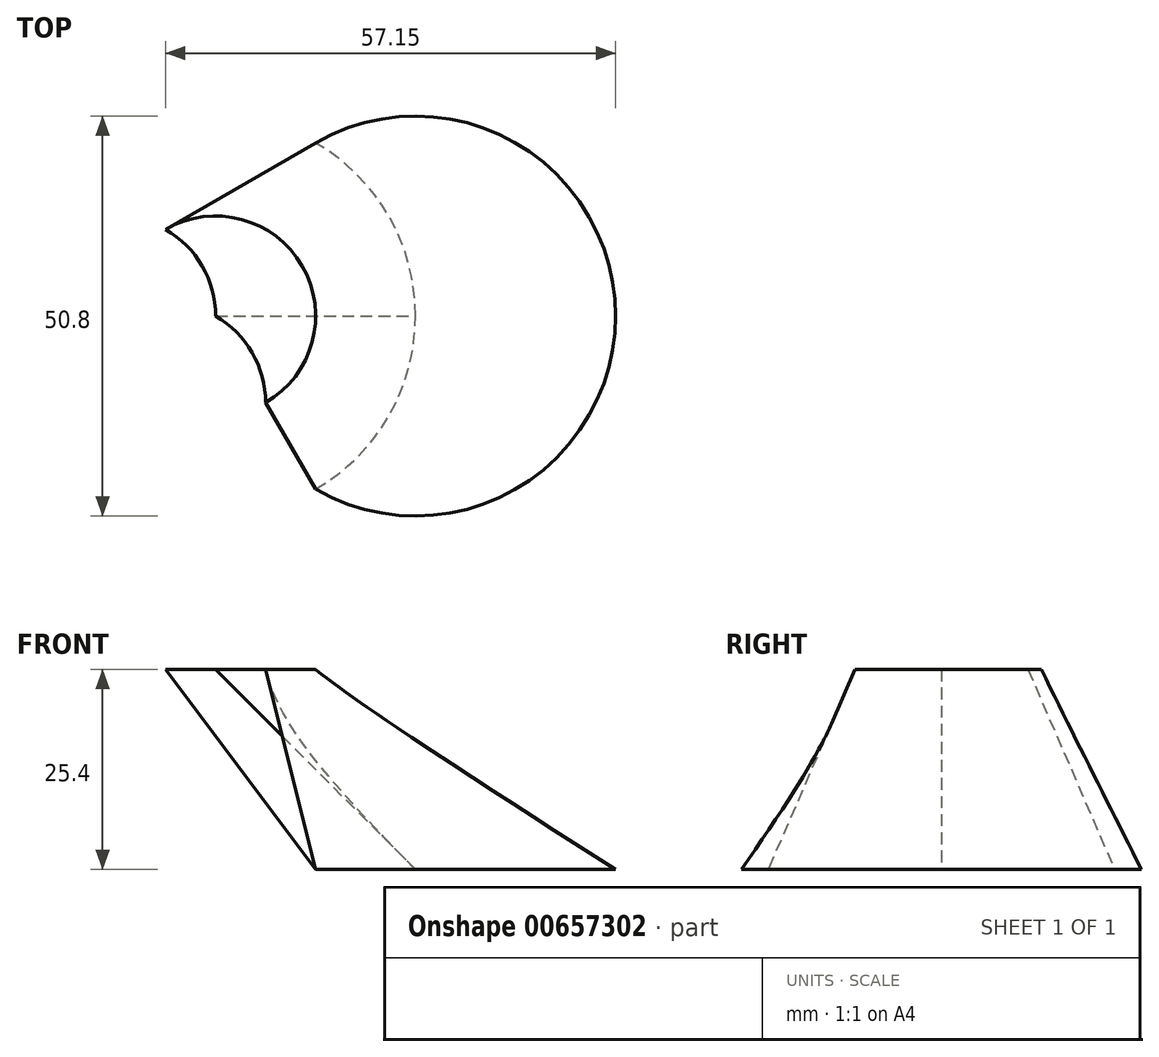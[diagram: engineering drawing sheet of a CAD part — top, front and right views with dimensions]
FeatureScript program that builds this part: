
annotation { "Feature Type Name" : "Feature", "Feature Type Description" : "" }
export const myFeature = defineFeature(function(context is Context, id is Id, definition is map)
    precondition{}
    {
        {
            var Q0;
            Q0=qCreatedBy(makeId("Top.planeOp"),FACE);
            var sketch = newSketch(context, id + "F0", { "sketchPlane" : qUnion([Q0])});
            skArc(sketch, "E0", {"start": v(-12.7, -22) * mm, "mid": v(25.4, 0) * mm, "end": v(-12.7, 22) * mm});
            skArc(sketch, "E1", {"start": v(-12.7, -22) * mm, "mid": v(0, 0) * mm, "end": v(-12.7, 22) * mm});
            skSolve(sketch);
        }
        {
            var Q0;
            Q0=qCreatedBy(makeId("Top.planeOp"),FACE);
            cPlane(context, id + "F1", {"entities" : qUnion([Q0]), "cplaneType" : CPlaneType.OFFSET, "offset" : 25.4 * mm, "width" : 152.4 * mm, "height" : 152.4 * mm});
        }
        {
            var Q0;
            Q0=qCreatedBy(id+"F1.planeOp",FACE);
            var sketch = newSketch(context, id + "F2", { "sketchPlane" : qUnion([Q0])});
            skPoint(sketch, "E2.0", {"position": v(-25.4, 0) * mm});
            skArc(sketch, "E3", {"start": v(-19.05, -11) * mm, "mid": v(-14.4, 6.35) * mm, "end": v(-31.75, 11) * mm});
            skArc(sketch, "E4", {"start": v(-25.4, 0) * mm, "mid": v(-27.1, 6.35) * mm, "end": v(-31.75, 11) * mm});
            skArc(sketch, "E5", {"start": v(-19.05, -11) * mm, "mid": v(-20.75, -4.65) * mm, "end": v(-25.4, 0) * mm});
            skSolve(sketch);
        }
        {
            var Q0;
            Q0=makeQuery(id+"F2.imprint","IMPRINT",FACE,{"disambiguationData":[TD([[makeQuery(id+"F2.imprint","IMPRINT",EDGE,{"derivedFrom":sQuery(id+"F2.wireOp",EDGE,"E3")}),1.0]])]});
            var Q1;
            Q1=makeQuery(id+"F0.imprint","IMPRINT",FACE,{"disambiguationData":[TD([[makeQuery(id+"F0.imprint","IMPRINT",EDGE,{"derivedFrom":sQuery(id+"F0.wireOp",EDGE,"E0")}),1.0]])]});
            loft(context, id + "F3", {"sheetProfilesArray" : [{ "sheetProfileEntities" : qUnion([Q0]) }, { "sheetProfileEntities" : qUnion([Q1]) }]});
        }
    });
